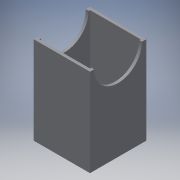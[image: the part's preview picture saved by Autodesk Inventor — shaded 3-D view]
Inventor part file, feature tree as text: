
AUTODESK INVENTOR PART (.ipt)
format: ipt  version: 2018 (Build 220112000, 112)  size: 118,272 bytes
history: native  units: mm
features: extrude x3, sketch x3
ambient origin geometry x8: Origin, YZ Plane, XZ Plane, XY Plane, X Axis, Y Axis, Z Axis, Center Point
bodies: Body1 (feature_tree)
feature tree (6):
  extrude  "押し出し3"  Depth=32.0mm
  extrude  "押し出し4"  Depth=32.0mm
  extrude  "押し出し5"  Depth=1.6mm
  sketch  "スケッチ5"
  sketch  "スケッチ6"
  sketch  "スケッチ7"
